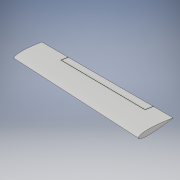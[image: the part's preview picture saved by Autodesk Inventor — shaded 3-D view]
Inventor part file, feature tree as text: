
AUTODESK INVENTOR PART (.ipt)
format: ipt  version: 2019.3 (Build 233278000, 278)  size: 189,952 bytes
history: native  units: mm
features: other x4, sketch x3, plane x3, loft x1, extrude x1
ambient origin geometry x8: Origin, YZ Plane, XZ Plane, XY Plane, X Axis, Y Axis, Z Axis, Center Point
bodies: Solid1 (feature_tree)
feature tree (12):
  sketch  "Sketch1"  dims[d0=0.0mm d1=10.0mm d2=0.0mm d3=10.0mm]
  plane  "Work Plane1"
  loft  "Loft1"
  extrude  "Extrusion1"  Depth=2437.5mm TaperAngle=0.0deg
  plane  "Work Plane2"
  plane  "Work Plane3"
  other  "2D Equation Curve1"
  other  "2D Equation Curve2"
  sketch  "Sketch2"  dims[d4=2437.5mm d5=0.0mm d6=10.0mm]
  other  "2D Equation Curve3"
  other  "2D Equation Curve4"
  sketch  "Sketch3"  dims[d7=0.0mm d8=10.0mm d9=0.0mm d10=90.0deg d11=0.0mm d12=90.0deg d13=365.625mm d14=1950.0mm d15=492.375mm d16=513.5mm d17=200.0mm d18=200.0mm d19=5.0mm d20=200.0mm d21=0.0mm d22=650.0mm d23=650.0mm]
